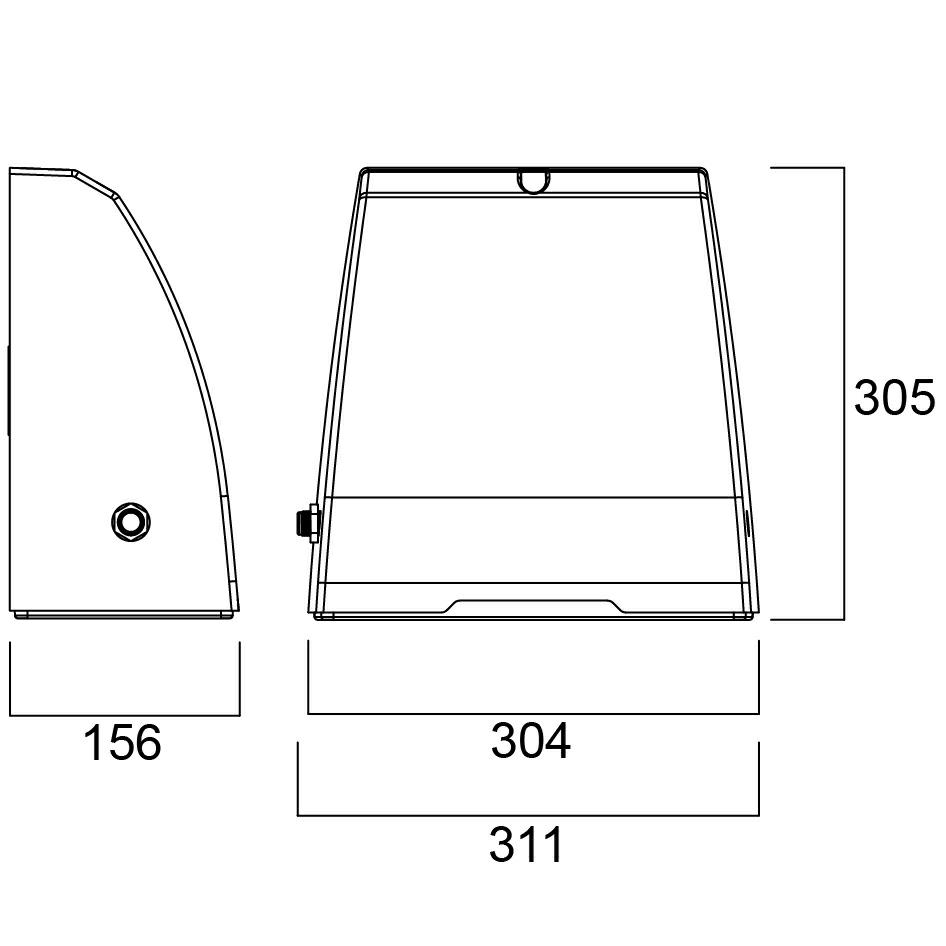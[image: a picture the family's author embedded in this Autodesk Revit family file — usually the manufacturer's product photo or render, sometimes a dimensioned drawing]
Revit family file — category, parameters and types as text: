
# Revit family: 0049944_2750lm
name_source: partatom
category: Lighting Fixtures
revit_build: Autodesk Revit 2018 (Build: 20170223_1515(x64)
units: mm (PartAtom-declared; Revit-internal decimal feet)

## family parameters
Cut with Voids When Loaded = No
Host = Face
Light Source = Yes
OmniClass Number = 23.80.70.00
OmniClass Title = Lighting
Part Type = Normal
Room Calculation Point = No
Round Connector Dimension = Use Diameter
Shared = No

## types (1)
- 0049944 MURO SURF IP65 1700-3250LM 840 PH GR
    Apparent Load = 28 VA
    Assembly Code = D5020200
    AssetType = Fixed
    ClassificationName = Uniclass2015
    ClassificationValue = EF_70_80
    Color Filter = 16777215
    Cost = 0 $
    Default Elevation = 1219 mm
    Description = Muro Surface is a wall mounted fixture for exterior lighting applications. Comes with aluminium housing in RAL7016 anthracite grey colour, frosted PC diffuser, IP65, IK10, Class I, 4000K, non-dimmable multipower driver with 5 settings, 1700 / 1900 / 2750 / 3150 / 3250 lm, 14 / 16 / 24 / 27 / 28 W, up to 121 lm/W total system efficacy, switchable built in Mini photocell, CRI80, Asymmetrical beam, 119.000 hrs L70B50 lifespan, 304 x 305 x 155 mm (L x W x D) dimensions, 4.1 kg weight.
    Dimming Lamp Color Temperature Shift = <None>
    DocumentationLiterature = http://www.sylvania-lighting.com
    ElectricShockClassification = 116
    Emit Shape Visible in Rendering = No
    Emit from Circle Diameter = 610 mm
    IfcExportAs = Class I
    IfcExportType = IfcLightFixtureType
    ImpactProtectionIndex = IfcLightFixtureType
    IngressProtection = IfcLightFixtureType
    InputNominalFrequency = 4000
    InputVoltage = 0
    LampColourRenderingIndex = 16500
    LampColourTemperature = LED
    LampMacAdamStep = 80
    LampNominalLuminous = 4000 K
    LightOutputRatio = LED
    LuminaireType = 0
    ManufacturerName = 116 lm/W
    Material = Feilo Sylvania
    Material_1_SYL = <By Category>
    Material_2_SYL = <By Category>
    Material_3_SYL = <By Category>
    Material_4_SYL = <By Category>
    Model = Muro Surface IP65 1700-3250lm 840 PH Grey
    ModelNumber = 0049944
    ModelReference = Muro Surface IP65 1700-3250lm 840 PH Grey
    Name = Muro Surface IP65 1700-3250lm 840 PH Grey
    NominalDepth = 155 mm  [stored 0.50853 ft]
    NominalHeight = 305 mm  [stored 1.00066 ft]
    NominalLength = 155 mm  [stored 0.50853 ft]
    Photometric Web File = 0049944_2750lm.IES
    PowerConsumption = Lighting
    PowerFactor = 0.95
    Tilt Angle = -90.00°
    Type Image = <None>
    TypeName = Muro Surface IP65 1700-3250lm 840 PH Grey
    URL = 0.9
    Voltage = 0 V
    WarrantyDescription = http://www.sylvania-lighting.com

note: [stored X ft] marks values corroborated as IEEE doubles in the binary element streams (Revit-internal decimal feet)

## geometry (parser evidence)
native form markers: Sweep x1
no freeform markers — native parametric forms only
